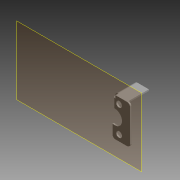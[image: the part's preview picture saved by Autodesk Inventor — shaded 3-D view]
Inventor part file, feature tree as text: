
AUTODESK INVENTOR PART (.ipt)
format: ipt  version: 2015 (Build 190159000, 159)  size: 137,216 bytes
history: native  units: mm (DEFAULTED — no unit token found)
features: sketch x4, other x3, hole x1, plane x1
ambient origin geometry x8: Origin, YZ Plane, XZ Plane, XY Plane, X Axis, Y Axis, Z Axis, Center Point
bodies: Solid1 (feature_tree)
feature tree (9):
  other  "endstopbrkt_CPY.ipt"
  hole  "Hole1"  [1 undecoded]
  other  "Solid1::endstopbrkt_CPY.ipt"
  other  "TaggingFeature1"
  sketch  "Sketch1"  dims[d0=10.0mm]
  sketch  "Sketch2"  dims[d1=4.0mm d2=4.0mm d3=3.0mm d4=6.0mm d5=4.0mm d6=2.0mm d7=90.0deg d8=0.5mm d9=20.594885mm]
  sketch  "Sketch3"
  sketch  "Sketch4"
  plane  "Work Plane1"
note: 1 required parameter value undecoded (feature->parameter linkage not recoverable at this tier; creation-order binding heuristic only, values carry confidence <= 0.55)
